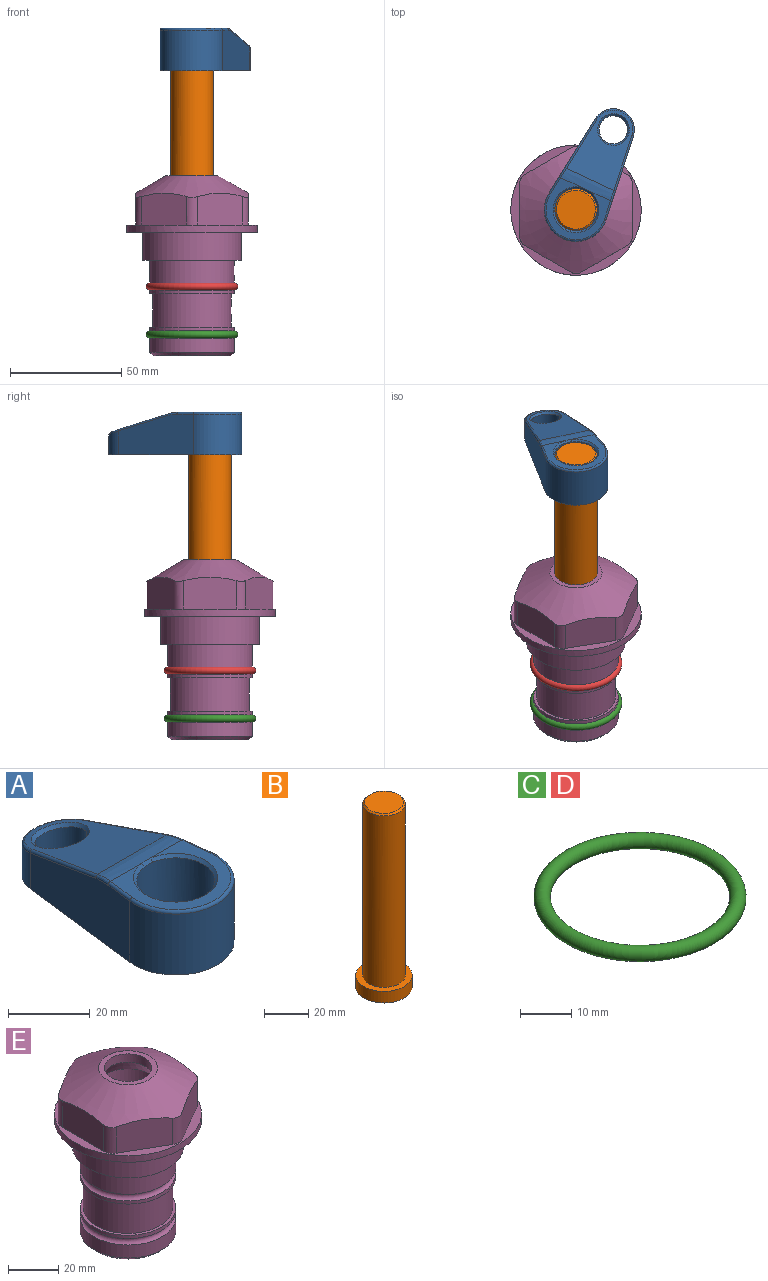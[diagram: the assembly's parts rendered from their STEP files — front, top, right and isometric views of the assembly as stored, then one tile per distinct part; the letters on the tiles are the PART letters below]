
ASSEMBLY  parts=5 mates=4
PART A: 31 faces, bbox 31.7x65.5x19.8 mm
  f0: plane 39.12x18.26mm, normal (0.99,0.12,0), area 612.2mm2, adj f1,f4,f7,f11,f13,f15
  f1: cylinder r=9.53mm len=18.91mm, axis (0,0,-1), area 296.1mm2, adj f0,f2,f7,f17
  f2: plane 39.12x18.26mm, normal (-0.99,0.12,0), area 612.2mm2, adj f1,f4,f7,f12,f14,f16
  f3: cylinder r=6.35mm len=12.7mm, axis (0,0,-1), area 362.4mm2, adj f7,f18
  f4: cylinder r=14.29mm len=28.58mm, axis (0,0,-1), area 882.2mm2, adj f0,f2,f7,f10
  f5: cylinder r=9.53mm len=19.05mm, axis (0,0,-1), area 1092.6mm2, adj f7,f19,f20
  f6: plane 26.99x23.69mm, normal (0,0,1), area 216.2mm2, adj f9,f10,f11,f12,f19
  f7: plane 63.5x28.58mm, normal (0,0,-1), area 661.8mm2, adj f0,f1,f2,f3,f4,f5,f22,f23
  f8: plane 33.52x23.6mm, normal (0,0.26,0.97), area 486mm2, adj f9,f15,f16,f17,f18
  f9: cylinder r=19.05mm len=24.72mm, axis (1,0,0), area 120.4mm2, adj f6,f8,f13,f14,f20
  f10: torus R=13.49mm, axis (0,0,1), area 59mm2, adj f4,f6,f11,f12
  f11: cylinder r=0.79mm len=8.67mm, axis (0.12,-0.99,0), area 10.8mm2, adj f0,f6,f10,f13
  f12: cylinder r=0.79mm len=8.67mm, axis (0.12,0.99,0), area 10.8mm2, adj f2,f6,f10,f14
  f13: bspline ~4.95x1.42mm, area 6.1mm2, adj f0,f9,f11,f15
  f14: bspline ~4.95x1.42mm, area 6.1mm2, adj f2,f9,f12,f16
  f15: cylinder r=0.79mm len=25.95mm, axis (0.12,-0.96,0.26), area 32.9mm2, adj f0,f8,f13,f17
  f16: cylinder r=0.79mm len=25.95mm, axis (0.12,0.96,-0.26), area 32.9mm2, adj f2,f8,f14,f17
  f17: bspline ~18.91x8.38mm, area 30mm2, adj f1,f8,f15,f16
  f18: bspline ~14.29x14.29mm, area 48.3mm2, adj f3,f8
  f19: cone r=9.53mm half-angle=45deg, axis (0,0,1), area 66.5mm2, adj f5,f6,f20
  f20: bspline ~3.22x0.96mm, area 3.5mm2, adj f5,f9,f19
  f21: plane 2.75x2.72mm, normal (0,0,-1), area 2.9mm2, adj f23,f25,f28
  f22: plane 23.05x15.88mm, normal (-0.99,-0.12,0), area 323.6mm2, adj f7,f25,f26,f27,f28,f29
  f23: plane 23.05x15.88mm, normal (0.99,-0.12,0), area 323.6mm2, adj f7,f21,f25,f27,f28,f30
  f24: cylinder r=9.53mm len=10.69mm, axis (0,0,-1), area 114.7mm2, adj f7,f27,f29,f30
  f25: cylinder r=12.7mm len=20.59mm, axis (0,0,-1), area 381.1mm2, adj f7,f21,f22,f23,f26,f28
  f26: plane 2.75x2.72mm, normal (0,0,-1), area 2.9mm2, adj f22,f25,f28
  f27: plane 19.72x18.37mm, normal (0,-0.26,-0.97), area 291.8mm2, adj f22,f23,f24,f28,f29,f30
  f28: cylinder r=15.88mm len=19.92mm, axis (1,0,0), area 54.8mm2, adj f21,f22,f23,f25,f26,f27
  f29: cylinder r=1.59mm len=11mm, axis (0,0,-1), area 34.7mm2, adj f7,f22,f24,f27
  f30: cylinder r=1.59mm len=11mm, axis (0,0,-1), area 34.7mm2, adj f7,f23,f24,f27
PART B: 6 faces, bbox 25.4x25.4x101.6 mm
  f0: plane 17.46x17.46mm, normal (0,0,1), area 239.5mm2, adj f5
  f1: plane 25.4x25.4mm, normal (0,0,-1), area 506.7mm2, adj f2
  f2: cylinder r=12.7mm len=25.4mm, axis (0,0,1), area 506.7mm2, adj f1,f3
  f3: plane 25.4x25.4mm, normal (0,0,1), area 221.7mm2, adj f2,f4
  f4: cylinder r=9.53mm len=94.46mm, axis (0,0,1), area 5653mm2, adj f3,f5
  f5: cone r=8.73mm half-angle=45deg, axis (0,0,-1), area 64.4mm2, adj f0,f4
PART C: 1 faces, bbox 44.7x44.7x3.2 mm
  f0: torus R=19.05mm, axis (0,0,1), area 1193.9mm2
PART D: same geometry as C
PART E: 36 faces, bbox 58.7x58.7x81 mm
  f0: cylinder r=17.78mm len=35.56mm, axis (0,0,1), area 1670.8mm2, adj f23,f24,f31
  f1: cylinder r=19.05mm len=38.1mm, axis (0,0,1), area 1191.9mm2, adj f26,f27,f30
  f2: plane 58.66x58.66mm, normal (0,0,-1), area 1150.6mm2, adj f3,f28
  f3: cylinder r=29.33mm len=58.66mm, axis (0,0,-1), area 585.1mm2, adj f2,f4
  f4: plane 58.66x58.66mm, normal (0,0,1), area 475.9mm2, adj f3,f5,f6,f7,f8,f9,f10,f11
  f5: plane 20.32x14.34mm, normal (-0.5,0.87,0), area 324.4mm2, adj f4,f15,f16,f17
  f6: plane 20.32x14.34mm, normal (0.5,0.87,0), area 324.4mm2, adj f4,f14,f15,f17
  f7: plane 23.48x14.34mm, normal (1,0,0), area 324.4mm2, adj f4,f13,f14,f17
  f8: plane 20.32x14.34mm, normal (0.5,-0.87,0), area 324.4mm2, adj f4,f12,f13,f17
  f9: plane 20.32x14.34mm, normal (-0.5,-0.87,0), area 324.4mm2, adj f4,f11,f12,f17
  f10: plane 23.48x14.34mm, normal (-1,0,0), area 324.4mm2, adj f4,f11,f16,f17
  f11: cylinder r=5.08mm len=12.85mm, axis (0,0,-1), area 67.2mm2, adj f4,f9,f10,f17
  f12: cylinder r=5.08mm len=12.85mm, axis (0,0,-1), area 67.2mm2, adj f4,f8,f9,f17
  f13: cylinder r=5.08mm len=12.85mm, axis (0,0,-1), area 67.2mm2, adj f4,f7,f8,f17
  f14: cylinder r=5.08mm len=12.85mm, axis (0,0,-1), area 67.2mm2, adj f4,f6,f7,f17
  f15: cylinder r=5.08mm len=12.85mm, axis (0,0,-1), area 67.2mm2, adj f4,f5,f6,f17
  f16: cylinder r=5.08mm len=12.85mm, axis (0,0,-1), area 67.2mm2, adj f4,f5,f10,f17
  f17: cone r=11.73mm half-angle=60deg, axis (0,0,-1), area 2071.8mm2, adj f5,f6,f7,f8,f9,f10,f11,f12
  f18: plane 23.46x23.46mm, normal (0,0,1), area 147.4mm2, adj f17,f35
  f19: plane 34.93x34.93mm, normal (0,0,-1), area 958mm2, adj f29
  f20: cylinder r=19.05mm len=38.1mm, axis (0,0,1), area 760.1mm2, adj f21,f29
  f21: torus R=19.05mm, axis (0,0,1), area 565.3mm2, adj f20,f22
  f22: cylinder r=19.05mm len=38.1mm, axis (0,0,1), area 190mm2, adj f21,f23
  f23: plane 38.1x38.1mm, normal (0,0,1), area 146.9mm2, adj f0,f22
  f24: plane 38.1x38.1mm, normal (0,0,-1), area 146.9mm2, adj f0,f25
  f25: cylinder r=19.05mm len=38.1mm, axis (0,0,1), area 190mm2, adj f24,f26
  f26: torus R=19.05mm, axis (0,0,1), area 565.3mm2, adj f1,f25
  f27: plane 44.45x44.45mm, normal (0,0,-1), area 411.7mm2, adj f1,f28
  f28: cylinder r=22.23mm len=44.45mm, axis (0,0,1), area 1773.5mm2, adj f2,f27
  f29: cone r=19.05mm half-angle=45deg, axis (0,0,1), area 257.5mm2, adj f19,f20
  f30: cylinder r=3.17mm len=6.75mm, axis (-1,0,0), area 128mm2, adj f1,f33
  f31: cylinder r=3.17mm len=6.35mm, axis (-1,0,0), area 102.5mm2, adj f0,f33
  f32: plane 25.4x25.4mm, normal (0,0,1), area 506.7mm2, adj f33
  f33: cylinder r=12.7mm len=66.42mm, axis (0,0,-1), area 5236.2mm2, adj f30,f31,f32,f34
  f34: cone r=9.53mm half-angle=30deg, axis (0,0,-1), area 443.4mm2, adj f33,f35
  f35: cylinder r=9.53mm len=19.05mm, axis (0,0,-1), area 240.9mm2, adj f18,f34
PLACE A rot(axis=(0,0,-1),25deg) t=(0,0,28.23)mm
PLACE B rot(axis=(0,0,-1),25deg) t=(0,0,27.43)mm
PLACE C t=(0,0,-21.59)mm
PLACE D at identity
PLACE E at identity fixed
MATE cylindrical E.f0 <-> B.f2  axis (0,0,1) through (0,0,-50.55)mm
MATE fastened A.f4 <-> B.f2  axis (0,0,1) through (0,0,90.93)mm
MATE fastened C.f0 <-> E.f0  axis (0,0,1) through (0,0,-46.1)mm
MATE fastened D.f0 <-> E.f0  axis (0,0,1) through (0,0,-24.51)mm
